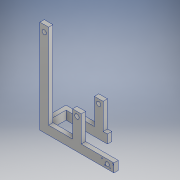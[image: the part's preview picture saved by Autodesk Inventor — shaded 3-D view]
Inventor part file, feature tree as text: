
AUTODESK INVENTOR PART (.ipt)
format: ipt  version: 2019 (Build 230136000, 136)  size: 223,232 bytes
history: native  units: in
note: dims shown in document units (in); Inventor stores cm internally (conversion verified against a paired STEP export)
features: sketch x9, extrude x5, hole x4, projected_geometry x2, plane x1, mirror x1
ambient origin geometry x8: Origin, YZ Plane, XZ Plane, XY Plane, X Axis, Y Axis, Z Axis, Center Point
bodies: Solid1 (feature_tree)
feature tree (22):
  extrude  "Extrusion1"  Depth=0.5in
  hole  "Hole2"  [1 undecoded]
  extrude  "Extrusion2"  Depth=0.5in
  extrude  "Extrusion3"  Depth=0.5in
  hole  "Hole6"  [1 undecoded]
  sketch  "3D Sketch1"
  plane  "Work Plane1"
  mirror  "Mirror1"
  hole  "Hole7"  [1 undecoded]
  extrude  "Extrusion4"  Depth=1.0in
  extrude  "Extrusion5"  TaperAngle=0.0deg  [1 undecoded]
  hole  "Hole8"  [1 undecoded]
  sketch  "Sketch3"  dims[d1=0.5in d4=0.5in]
  projected_geometry  "Projected Loop1"
  sketch  "Sketch5"  dims[d6=1.0in d7=0.0in d18=1.0in]
  sketch  "Sketch8"  dims[d19=0.5in d20=1.25in]
  sketch  "Sketch9"  dims[d21=0.472in d22=0.75in d23=0.375in d24=0.25in d25=0.5635in d26=1.0in d27=0.8108in d39=0.5in]
  sketch  "Sketch10"  dims[d41=9.75in d42=0.0in d63=0.5in]
  sketch  "Sketch11"  dims[d64=9.0in d65=9.0in]
  sketch  "Sketch12"  dims[d66=2.0in d67=1.0in]
  projected_geometry  "Projected Loop5"
  sketch  "Sketch13"  dims[d68=0.0in d69=0.0in d70=0.75in d71=1.0in d72=0.5in d73=0.5in d74=0.75in d75=0.375in d76=0.25in d77=0.5635in d78=1.0in d79=0.8108in d81=1.0in d83=0.5in d84=0.5in d85=2.75in d86=3.0in d87=0.0in d89=1.0in d90=0.5in d91=0.5in d92=0.505in d93=0.75in d94=0.375in d95=0.25in d96=0.5635in d97=1.0in d98=0.8108in d99=0.5in d100=2.0in d101=0.0in d102=0.5in d103=2.0in d104=0.0in d105=0.305in d106=0.253in d107=0.276in d108=0.61in d109=0.61in d110=0.276in d111=0.305in d112=0.253in d113=0.125in d114=0.25in d115=0.119in d116=0.25in d117=0.5635in d118=1.0in d119=0.8108in d120=0.375in]
note: 5 required parameter values undecoded (feature->parameter linkage not recoverable at this tier; creation-order binding heuristic only, values carry confidence <= 0.55)
